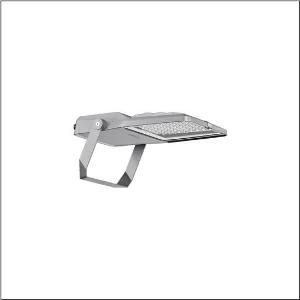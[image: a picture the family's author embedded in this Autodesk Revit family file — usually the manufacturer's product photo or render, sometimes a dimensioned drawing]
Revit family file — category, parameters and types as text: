
# Revit family: floodlight_fl_21_iq_mini___pl43_5xa7772c5a1a_be68
name_source: partatom
category: Lighting Fixtures
units: mm (PartAtom-declared; Revit-internal decimal feet)

## family parameters
Cut with Voids When Loaded = No
Host = Face
Light Source = No
Part Type = Normal
Room Calculation Point = No
Round Connector Dimension = Use Diameter
Shared = No

## types (1)
- --- (1 x LED, 11690 lm, 87.2 W, 4000K)
    Apparent Load = 87 VA
    CIE Flux Codes = 27 78 99 100 100
    Color Rendering = 80
    Color Temperature = 4000K
    Default Elevation = 1800 mm
    Description = Floodlight FL 21 iQ mini, floodlight, primary light control with lens, of PMMA, primary optical cover: protective disc, of toughened safety glass, transparent, light distribution: PL43, light emission: direct distribution, installation type: surface-mounted, LED, High Power LED, rated luminous flux: 11.690lm, luminous efficacy: 134lm/W, light colour: 840, colour temperature: 4000K, control: Street-Remote, Auto-Match, Temp-Guard, Night-Set, Smart-Wire, Desk-Remote (wireless, voltage-free reading and setting of iQ features in the workshop via application-optimized NFC function/RFID function), optimised constant luminous flux control (CLO 2.0), with terminal, 6-pole, mains connection: 220..240V, AC, 50/60Hz, start of lifetime: 87W, end of service life: 92W, reduction: 40W, luminaire housing, of diecast aluminium, powder-coated, Siteco® metallic grey (DB 702S), corrosivity category C5 mid according to DIN EN ISO 12944, sealing non-destructively replaceable, mounting bracket, of steel, galvanised, powder-coated, Siteco® metallic grey (DB 702S), protection rating (complete): IP66, insulation class (complete): insulation class II (safety insulation), certification: CE, ENEC, VDE, protection symbol: D, impact resistance: IK08, permissible operating ambient temperature: -40..+40°C, permissible operating ambient temperature for outdoor applications: -40..+50°C, standard: DIN EN 12944, LABS conformity tested according to VDMA 24364:2018-05, packaging unit: 1 piece

Light Distribution: PL43
    Height = 70 mm
    Lamp = 1 x LED
    Lamp Light Flux = 11690 lm
    Lamp Power = 87.2 W
    Lamp count = 1
    Length = 485 mm
    Luminous efficacy = 134 lm/W
    Manufacturer = Siteco
    ModVariant = No
    Model = 5XA7772C5A1A
    Number of Poles = 1
    OnlyDefault = Yes
    Power Factor = 1
    Product Name = Floodlight FL 21 iQ mini | PL43
    Product group = floodlight | pylon annexe
    ProductGroupID = 6200
    Protection Class = Protection class II
    Protection Degree = IP 66
    RLX_Detail_Level = 1
    RLX_Emergency_Light_Flux = 0 lm
    RLX_Emergency_Type = 0
    RLX_Emergency_Type_DB = No
    RlxData = <blob elided: 96117 chars, md5=911d18a9>
    Socket = socket
    Standby Power = 0 W
    System Light Flux = 11690 lm
    System Power = 87 W
    Type Comments = factory setting: luminous flux: 100 % | dim-lin: 254 | 456 mA
    Type Image = l_1006845.jpg
    URL = http://relux.com
    VarID = @adj_112277
    Voltage = 0 V
    Weight = 0.00 kg
    Width = 337 mm

## geometry (parser evidence)
native form markers: Blend x4, Sweep x11
no freeform markers — native parametric forms only
